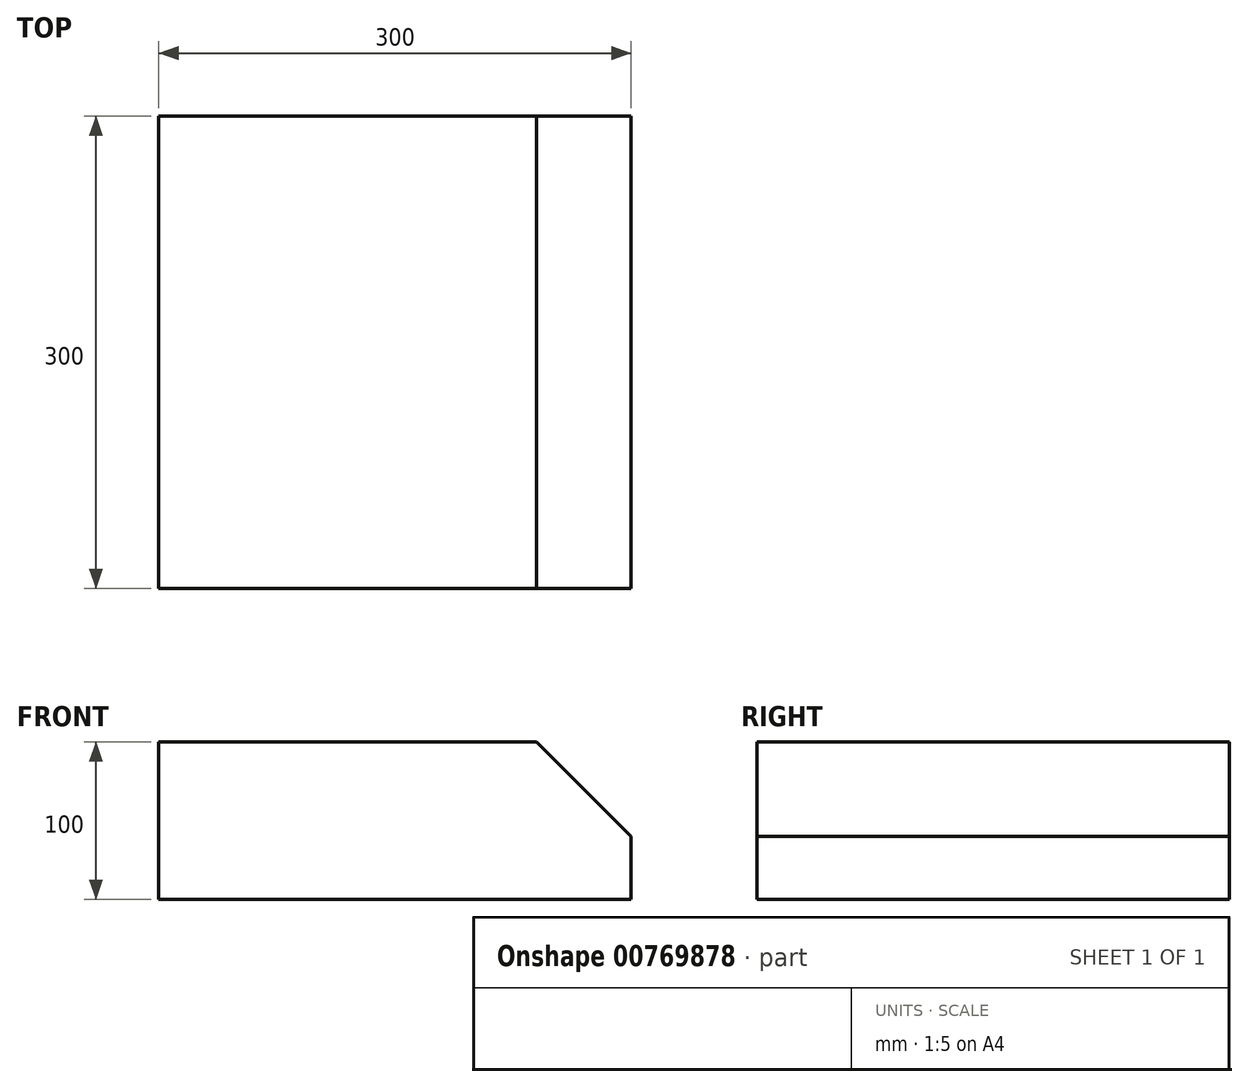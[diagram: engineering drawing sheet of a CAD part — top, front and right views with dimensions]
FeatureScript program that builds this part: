
annotation { "Feature Type Name" : "Feature", "Feature Type Description" : "" }
export const myFeature = defineFeature(function(context is Context, id is Id, definition is map)
    precondition{}
    {
        {
            var Q0;
            Q0=qCreatedBy(makeId("Front.planeOp"),FACE);
            var sketch = newSketch(context, id + "F0", { "sketchPlane" : qUnion([Q0])});
            skLineSegment(sketch, "E0", {"start": v(0, 0) * mm, "end": v(-300, 0) * mm});
            skLineSegment(sketch, "E1", {"start": v(-300, 0) * mm, "end": v(-300, 100) * mm});
            skLineSegment(sketch, "E2", {"start": v(-300, 100) * mm, "end": v(-60, 100) * mm});
            skLineSegment(sketch, "E3", {"start": v(-60, 100) * mm, "end": v(0, 40) * mm});
            skLineSegment(sketch, "E4", {"start": v(0, 40) * mm, "end": v(0, 0) * mm});
            skSolve(sketch);
        }
        {
            var Q0;
            Q0 = qSketchRegion(id + "F0", true);
            extrude(context, id + "F1", {"entities" : qUnion([Q0]), "endBound" : BoundingType.SYMMETRIC, "depth" : 300 * mm, "offsetDistance" : 25 * mm});
        }
    });
